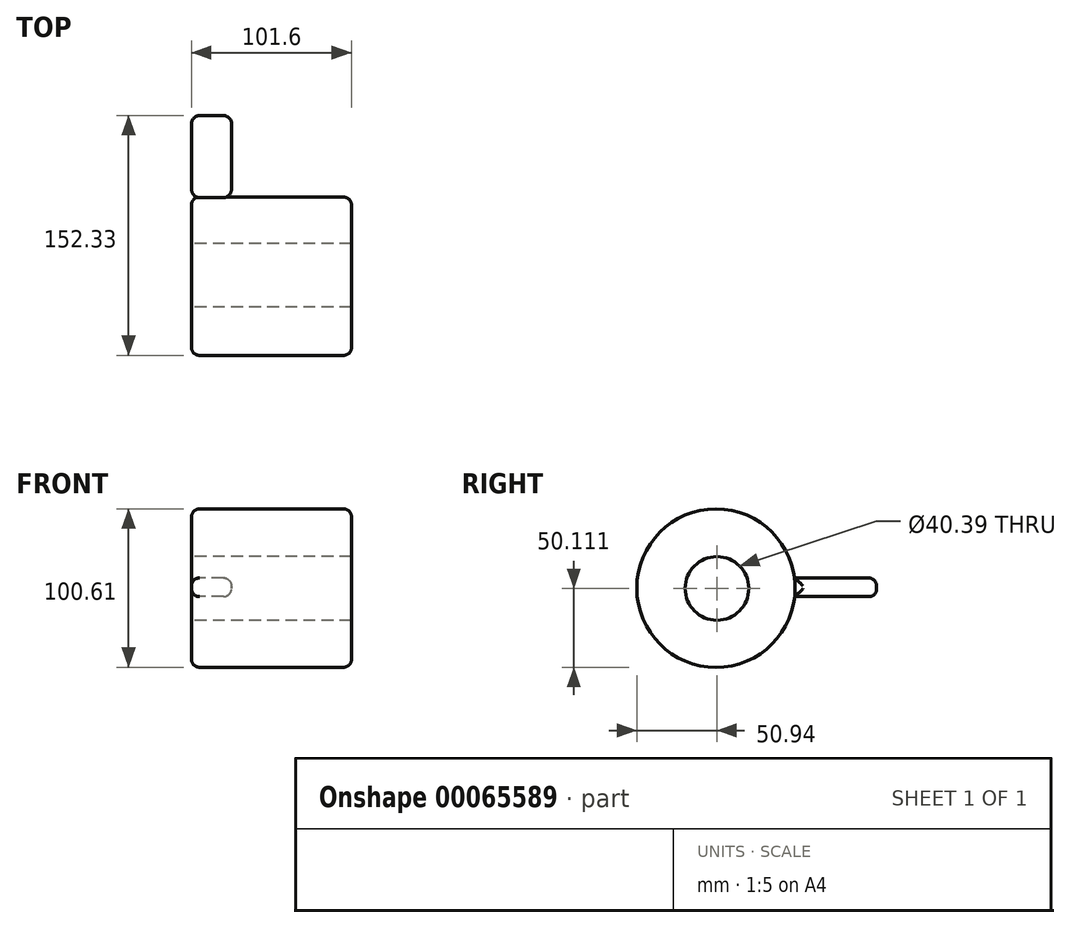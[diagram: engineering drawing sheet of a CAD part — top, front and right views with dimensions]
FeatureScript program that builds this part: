
annotation { "Feature Type Name" : "Feature", "Feature Type Description" : "" }
export const myFeature = defineFeature(function(context is Context, id is Id, definition is map)
    precondition{}
    {
        {
            var Q0;
            Q0=qCreatedBy(makeId("Right.planeOp"),FACE);
            var sketch = newSketch(context, id + "F0", { "sketchPlane" : qUnion([Q0])});
            skCircle(sketch, "E0", {"center": v(0, 32.9) * mm, "radius": 20.2 * mm});
            skCircle(sketch, "E1", {"center": v(-0.63, 33.1) * mm, "radius": 50.3 * mm});
            skSolve(sketch);
        }
        {
            var Q0;
            Q0=makeQuery(id+"F0.imprint","IMPRINT",FACE,{"disambiguationData":[TD([[makeQuery(id+"F0.imprint","IMPRINT",EDGE,{"derivedFrom":sQuery(id+"F0.wireOp",EDGE,"E0")}),-1.0]])]});
            extrude(context, id + "F1", {"entities" : qUnion([Q0]), "depth" : 101.6 * mm});
        }
        {
            var Q0;
            Q0=makeQuery(id+"F0.imprint","IMPRINT",FACE,{"disambiguationData":[TD([[makeQuery(id+"F0.imprint","IMPRINT",EDGE,{"derivedFrom":sQuery(id+"F0.wireOp",EDGE,"E0")}),-1.0]])]});
            var sketch = newSketch(context, id + "F2", { "sketchPlane" : qUnion([Q0])});
            skLineSegment(sketch, "E2.bottom", {"start": v(-19.85, 68.72) * mm, "end": v(116.36, 68.72) * mm});
            skLineSegment(sketch, "E2.top", {"start": v(-19.85, 59.87) * mm, "end": v(116.36, 59.87) * mm});
            skLineSegment(sketch, "E2.left", {"start": v(-19.85, 68.72) * mm, "end": v(-19.85, 59.87) * mm});
            skLineSegment(sketch, "E2.right", {"start": v(116.36, 68.72) * mm, "end": v(116.36, 59.87) * mm});
            skLineSegment(sketch, "E3.bottom", {"start": v(49.25, 39.55) * mm, "end": v(101.39, 39.55) * mm});
            skLineSegment(sketch, "E3.top", {"start": v(49.25, 27.69) * mm, "end": v(101.39, 27.69) * mm});
            skLineSegment(sketch, "E3.left", {"start": v(49.25, 39.55) * mm, "end": v(49.25, 27.69) * mm});
            skLineSegment(sketch, "E3.right", {"start": v(101.39, 39.55) * mm, "end": v(101.39, 27.69) * mm});
            skSolve(sketch);
        }
        {
            var Q0;
            {var subQ0=sQuery(id+"F2.wireOp",EDGE,"E3.right");Q0=makeQuery(id+"F2.imprint","IMPRINT",FACE,{"disambiguationData":[TD([[makeQuery(id+"F2.imprint","IMPRINT",EDGE,{"derivedFrom":subQ0}),-1.0]])]});}
            extrude(context, id + "F3", {"entities" : qUnion([Q0]), "depth" : 25.4 * mm});
        }
        {
            var Q0;
            Q0=makeQuery(id+"F3.opExtrude","SWEPT_FACE",FACE,{"disambiguationData":[OSD([sQuery(id+"F2.wireOp",EDGE,"E3.right")])]});
            var Q1;
            Q1=makeQuery(id+"F3.opExtrude","CAP_FACE",FACE,{"disambiguationData":[OSD([sQuery(id+"F0.wireOp",EDGE,"E1"),sQuery(id+"F2.wireOp",EDGE,"E3.bottom"),sQuery(id+"F2.wireOp",EDGE,"E3.top"),sQuery(id+"F2.wireOp",EDGE,"E3.right")])],"isStart":false});
            var Q2;
            Q2=makeQuery(id+"F3.opExtrude","CAP_FACE",FACE,{"disambiguationData":[OSD([sQuery(id+"F0.wireOp",EDGE,"E1"),sQuery(id+"F2.wireOp",EDGE,"E3.bottom"),sQuery(id+"F2.wireOp",EDGE,"E3.top"),sQuery(id+"F2.wireOp",EDGE,"E3.right")])],"isStart":true});
            var Q3;
            Q3=makeQuery(id+"F1.opExtrude","CAP_EDGE",EDGE,{"disambiguationData":[OSD([sQuery(id+"F0.wireOp",EDGE,"E1")])],"isStart":true});
            var Q4;
            Q4=makeQuery(id+"F1.opExtrude","SWEPT_FACE",FACE,{"disambiguationData":[OSD([sQuery(id+"F0.wireOp",EDGE,"E1")])]});
            fillet(context, id + "F4", {"entities" : qUnion([Q0, Q1, Q2, Q3, Q4]), "radius" : 5.08 * mm, "tangentPropagation" : true, "allowEdgeOverflow" : false});
        }
    });
